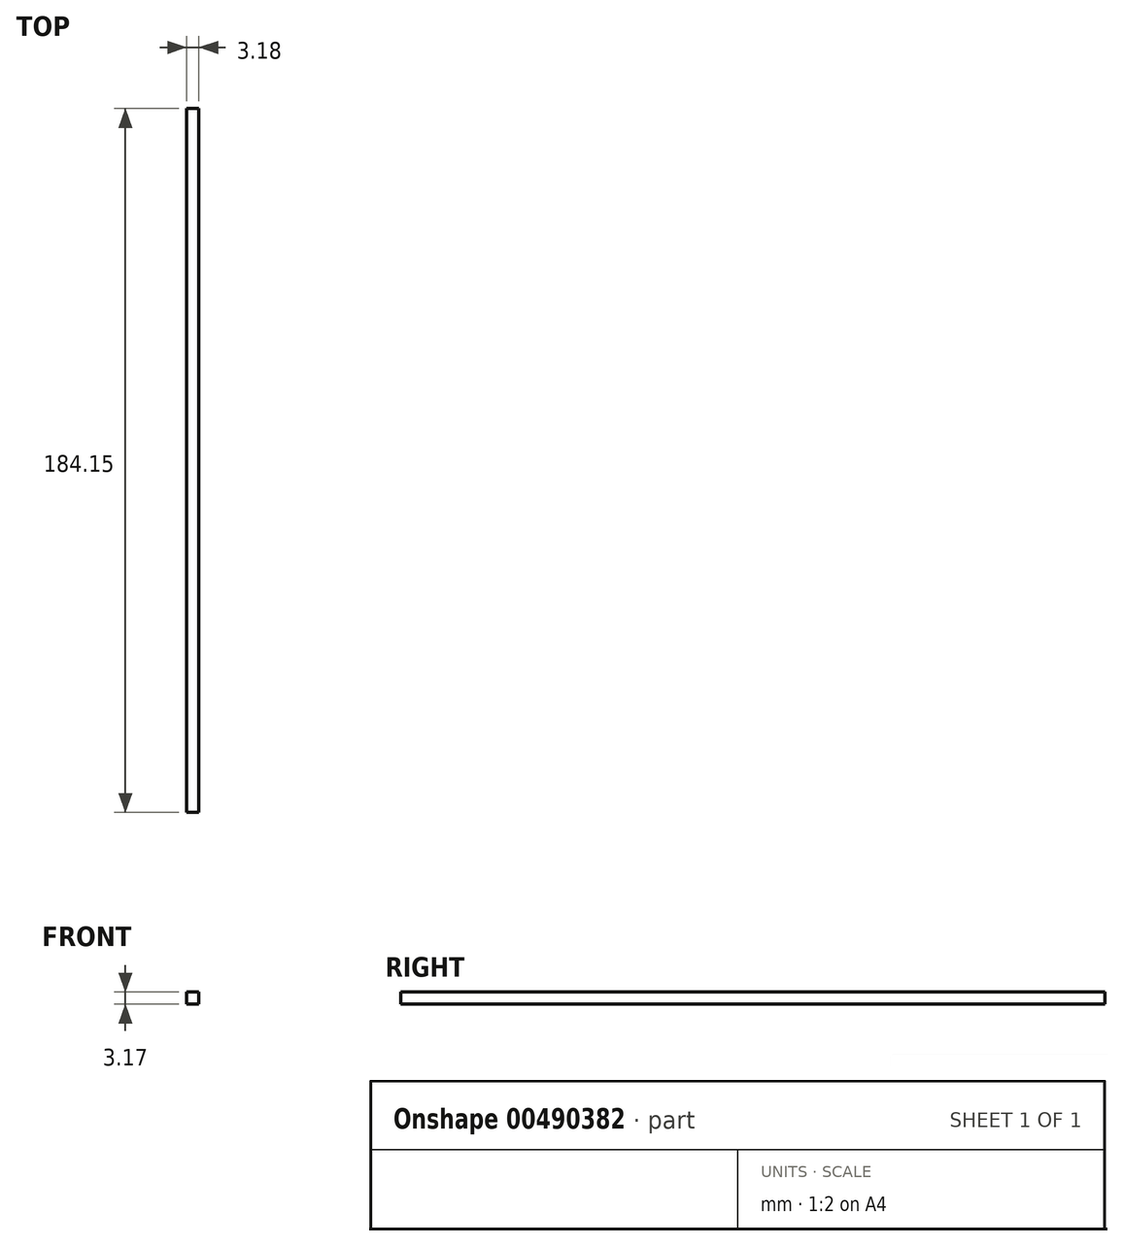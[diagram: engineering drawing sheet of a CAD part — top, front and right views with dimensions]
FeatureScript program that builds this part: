
annotation { "Feature Type Name" : "Feature", "Feature Type Description" : "" }
export const myFeature = defineFeature(function(context is Context, id is Id, definition is map)
    precondition{}
    {
        {
            var Q0;
            Q0=qCreatedBy(makeId("Front.planeOp"),FACE);
            var sketch = newSketch(context, id + "F0", { "sketchPlane" : qUnion([Q0])});
            skLineSegment(sketch, "E0.bottom", {"start": v(-51.43, 38.28) * mm, "end": v(-48.25, 38.28) * mm});
            skLineSegment(sketch, "E0.top", {"start": v(-51.43, 35.1) * mm, "end": v(-48.25, 35.1) * mm});
            skLineSegment(sketch, "E0.left", {"start": v(-51.43, 38.28) * mm, "end": v(-51.43, 35.1) * mm});
            skLineSegment(sketch, "E0.right", {"start": v(-48.25, 38.28) * mm, "end": v(-48.25, 35.1) * mm});
            skSolve(sketch);
        }
        {
            var Q0;
            Q0 = qSketchRegion(id + "F0", true);
            extrude(context, id + "F1", {"entities" : qUnion([Q0]), "depth" : 184.15 * mm});
        }
    });
